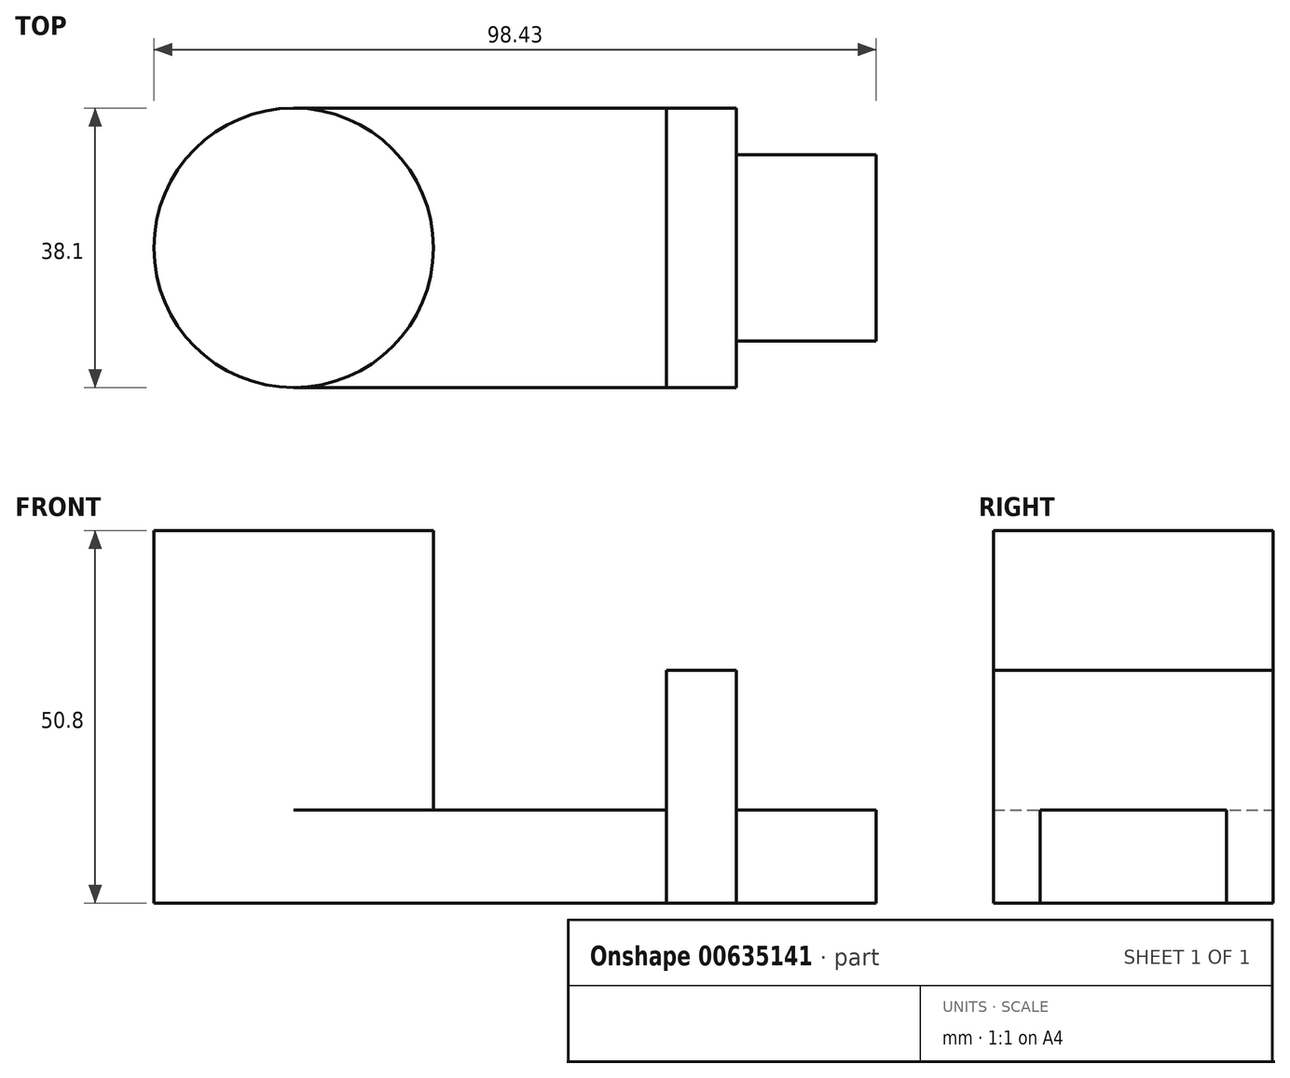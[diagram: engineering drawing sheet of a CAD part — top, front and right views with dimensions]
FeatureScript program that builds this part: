
annotation { "Feature Type Name" : "Feature", "Feature Type Description" : "" }
export const myFeature = defineFeature(function(context is Context, id is Id, definition is map)
    precondition{}
    {
        {
            var Q0;
            Q0=qCreatedBy(makeId("Top.planeOp"),FACE);
            var sketch = newSketch(context, id + "F0", { "sketchPlane" : qUnion([Q0])});
            skCircle(sketch, "E0", {"center": v(0, 0) * mm, "radius": 19.05 * mm});
            skLineSegment(sketch, "E1.bottom", {"start": v(0, 19.05) * mm, "end": v(50.8, 19.05) * mm});
            skLineSegment(sketch, "E1.top", {"start": v(0, -19.05) * mm, "end": v(50.8, -19.05) * mm});
            skLineSegment(sketch, "E1.left", {"start": v(0, 19.05) * mm, "end": v(0, -19.05) * mm});
            skLineSegment(sketch, "E1.right", {"start": v(50.8, 19.05) * mm, "end": v(50.8, -19.05) * mm});
            skLineSegment(sketch, "E2.bottom", {"start": v(50.8, 19.05) * mm, "end": v(60.33, 19.05) * mm});
            skLineSegment(sketch, "E2.top", {"start": v(50.8, -19.05) * mm, "end": v(60.33, -19.05) * mm});
            skLineSegment(sketch, "E2.right", {"start": v(60.33, 19.05) * mm, "end": v(60.33, -19.05) * mm});
            skLineSegment(sketch, "E3.bottom", {"start": v(60.33, -12.7) * mm, "end": v(79.38, -12.7) * mm});
            skLineSegment(sketch, "E3.top", {"start": v(60.33, 12.7) * mm, "end": v(79.38, 12.7) * mm});
            skLineSegment(sketch, "E3.left", {"start": v(60.33, -12.7) * mm, "end": v(60.33, 12.7) * mm});
            skLineSegment(sketch, "E3.right", {"start": v(79.38, -12.7) * mm, "end": v(79.38, 12.7) * mm});
            skSolve(sketch);
        }
        {
            var Q0;
            {var subQ0=sQuery(id+"F0.wireOp",EDGE,"E1.left");Q0=makeQuery(id+"F0.imprint","IMPRINT",FACE,{"disambiguationData":[TD([[makeQuery(id+"F0.imprint","IMPRINT",EDGE,{"derivedFrom":subQ0}),1.0]])]});}
            var Q1;
            {var subQ0=sQuery(id+"F0.wireOp",EDGE,"E1.left");Q1=makeQuery(id+"F0.imprint","IMPRINT",FACE,{"disambiguationData":[TD([[makeQuery(id+"F0.imprint","IMPRINT",EDGE,{"derivedFrom":subQ0}),-1.0]])]});}
            extrude(context, id + "F1", {"entities" : qUnion([Q0, Q1]), "depth" : 50.8 * mm, "offsetDistance" : 25.4 * mm});
        }
        {
            var Q0;
            {var subQ1=sQuery(id+"F0.wireOp",EDGE,"E1.bottom");Q0=makeQuery(id+"F0.imprint","IMPRINT",FACE,{"disambiguationData":[TD([[makeQuery(id+"F0.imprint","IMPRINT",EDGE,{"derivedFrom":subQ1}),-1.0]])]});}
            var Q1;
            Q1=makeQuery(id+"F0.imprint","IMPRINT",FACE,{"disambiguationData":[TD([[makeQuery(id+"F0.imprint","IMPRINT",EDGE,{"derivedFrom":sQuery(id+"F0.wireOp",EDGE,"E3.bottom")}),1.0]])]});
            extrude(context, id + "F2", {"entities" : qUnion([Q0, Q1]), "operationType" : NewBodyOperationType.ADD, "depth" : 12.7 * mm, "offsetDistance" : 25.4 * mm});
        }
        {
            var Q0;
            {var subQ1=sQuery(id+"F0.wireOp",EDGE,"E2.bottom");Q0=makeQuery(id+"F0.imprint","IMPRINT",FACE,{"disambiguationData":[TD([[makeQuery(id+"F0.imprint","IMPRINT",EDGE,{"derivedFrom":subQ1}),-1.0]])]});}
            extrude(context, id + "F3", {"entities" : qUnion([Q0]), "depth" : 31.75 * mm, "offsetDistance" : 25.4 * mm});
        }
    });
